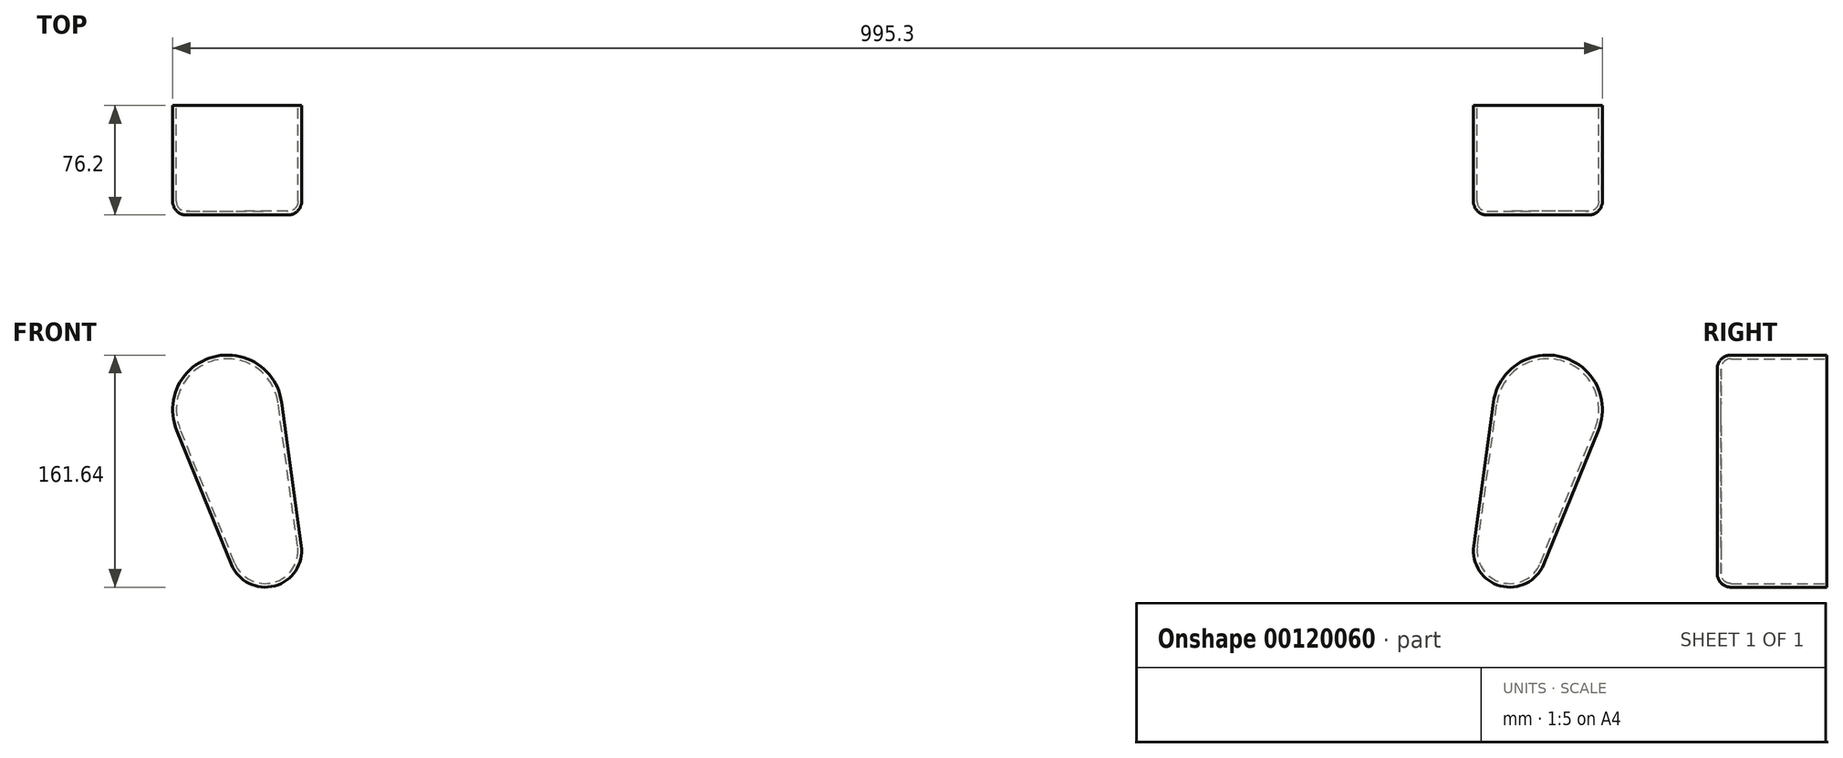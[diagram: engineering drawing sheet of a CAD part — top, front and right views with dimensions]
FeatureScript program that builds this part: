
annotation { "Feature Type Name" : "Feature", "Feature Type Description" : "" }
export const myFeature = defineFeature(function(context is Context, id is Id, definition is map)
    precondition{}
    {
        {
            var Q0;
            Q0=qCreatedBy(makeId("Front.planeOp"),FACE);
            var sketch = newSketch(context, id + "F0", { "sketchPlane" : qUnion([Q0])});
            skArc(sketch, "E0", {"start": v(37.8, -4.76) * mm, "mid": v(0, 38.1) * mm, "end": v(-37.8, -4.76) * mm});
            skArc(sketch, "E1", {"start": v(-25.2, -104.77) * mm, "mid": v(0, -127) * mm, "end": v(25.2, -104.78) * mm});
            skLineSegment(sketch, "E2", {"start": v(-25.2, -104.78) * mm, "end": v(-37.8, -4.76) * mm});
            skLineSegment(sketch, "E3", {"start": v(25.2, -104.78) * mm, "end": v(37.8, -4.76) * mm});
            skPoint(sketch, "E4.orphan", {"position": v(-38.4, 0) * mm});
            skPoint(sketch, "E5.orphan", {"position": v(38.4, 0) * mm});
            skSolve(sketch);
        }
        {
            var Q0;
            Q0=makeQuery(id+"F0.imprint","IMPRINT",FACE,{"disambiguationData":[TD([[makeQuery(id+"F0.imprint","IMPRINT",EDGE,{"derivedFrom":sQuery(id+"F0.wireOp",EDGE,"E0")}),1.0]])]});
            extrude(context, id + "F1", {"entities" : qUnion([Q0]), "depth" : 76.2 * mm});
        }
        {
            var Q0;
            Q0=makeQuery(id+"F1.opExtrude","CAP_EDGE",EDGE,{"disambiguationData":[OSD([sQuery(id+"F0.wireOp",EDGE,"E2")])],"isStart":false});
            fillet(context, id + "F2", {"entities" : qUnion([Q0]), "radius" : 9.52 * mm, "tangentPropagation" : true, "allowEdgeOverflow" : false});
        }
        {
            var Q0;
            Q0=makeQuery(id+"F1.opExtrude","CAP_FACE",FACE,{"disambiguationData":[OSD([sQuery(id+"F0.wireOp",EDGE,"E0"),sQuery(id+"F0.wireOp",EDGE,"E1"),sQuery(id+"F0.wireOp",EDGE,"E2"),sQuery(id+"F0.wireOp",EDGE,"E3")])],"isStart":true});
            shell(context, id + "F3", {"entities" : qUnion([Q0]), "thickness" : 2.54 * mm});
        }
        {
            var Q0;
            Q0=makeQuery(id+"F1.opExtrude","SWEPT_BODY",BODY,{"disambiguationData":[OSD([sQuery(id+"F0.wireOp",EDGE,"E0"),sQuery(id+"F0.wireOp",EDGE,"E1"),sQuery(id+"F0.wireOp",EDGE,"E2"),sQuery(id+"F0.wireOp",EDGE,"E3")])]});
            var Q1;
            {var subQ0=sQuery(id+"F0.wireOp",EDGE,"E3");var subQ1=sQuery(id+"F0.wireOp",EDGE,"E0");Q1=makeQuery(id+"F3.opShell","OFFSET_EDGE",EDGE,{"disambiguationData":[OSD([subQ1,subQ0]),TDD([makeQuery(id+"F1.opExtrude","SWEPT_EDGE",EDGE,{"disambiguationData":[OSD([subQ1,subQ0])]})])]});}
            transform(context, id + "F4", {"entities" : qUnion([Q0]), "transformType" : TransformType.ROTATION, "transformAxis" : qUnion([Q1]), "angle" : 15 * degree, "makeCopy" : false});
        }
        {
            var Q0;
            Q0=qCreatedBy(makeId("Right.planeOp"),FACE);
            cPlane(context, id + "F5", {"entities" : qUnion([Q0]), "cplaneType" : CPlaneType.OFFSET, "offset" : 457.2 * mm, "oppositeDirection" : true, "width" : 152.4 * mm, "height" : 152.4 * mm});
        }
        {
            var Q0;
            Q0=makeQuery(id+"F1.opExtrude","SWEPT_BODY",BODY,{"disambiguationData":[OSD([sQuery(id+"F0.wireOp",EDGE,"E0"),sQuery(id+"F0.wireOp",EDGE,"E1"),sQuery(id+"F0.wireOp",EDGE,"E2"),sQuery(id+"F0.wireOp",EDGE,"E3")])]});
            var Q1;
            Q1=qCreatedBy(id+"F5.planeOp",FACE);
            mirror(context, id + "F6", {"operationType" : NewBodyOperationType.ADD, "entities" : qUnion([Q0]), "mirrorPlane" : qUnion([Q1])});
        }
    });
